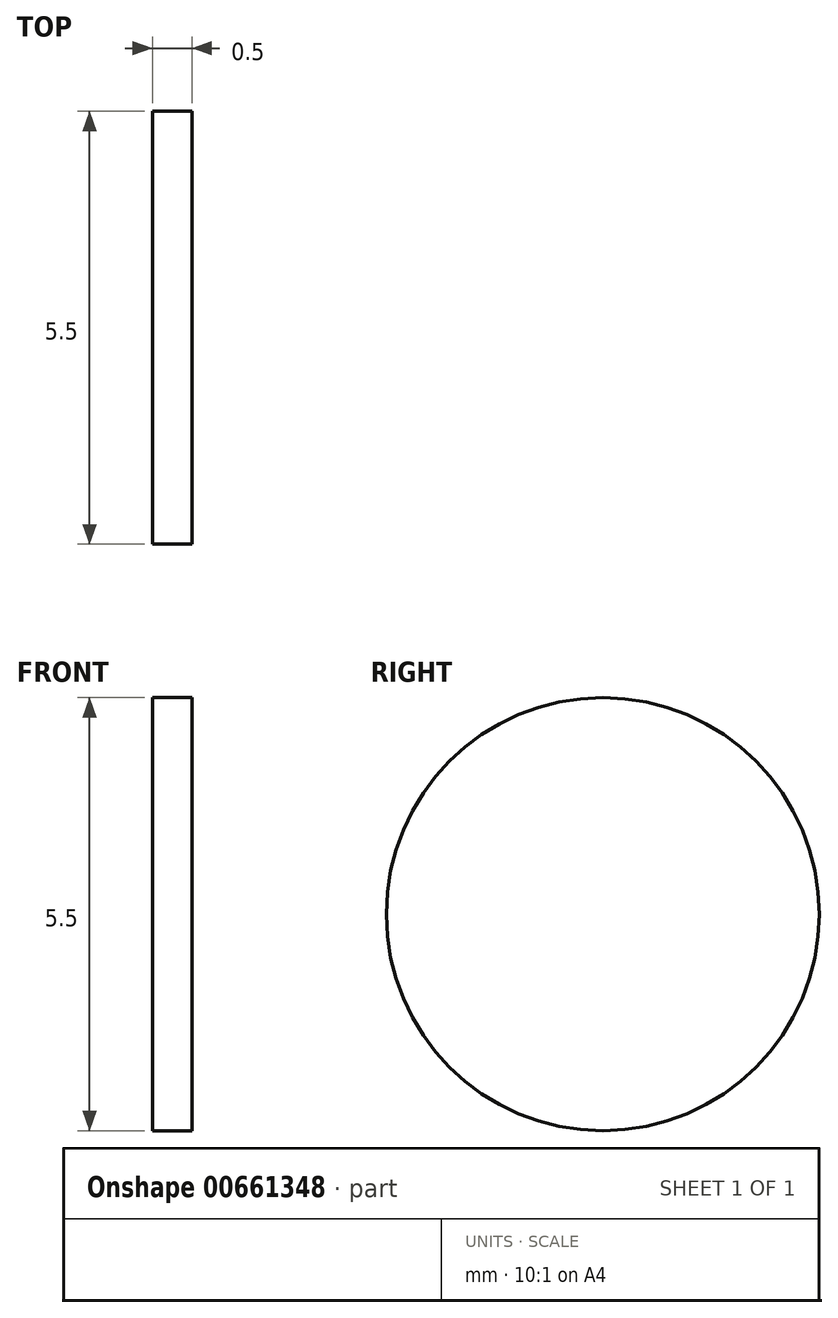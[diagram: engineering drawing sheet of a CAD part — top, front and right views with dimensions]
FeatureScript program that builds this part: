
annotation { "Feature Type Name" : "Feature", "Feature Type Description" : "" }
export const myFeature = defineFeature(function(context is Context, id is Id, definition is map)
    precondition{}
    {
        {
            var Q0;
            Q0=qCreatedBy(makeId("Right.planeOp"),FACE);
            var sketch = newSketch(context, id + "F0", { "sketchPlane" : qUnion([Q0])});
            skCircle(sketch, "E0", {"center": v(0, 0) * mm, "radius": 2.75 * mm});
            skSolve(sketch);
        }
        {
            var Q0;
            Q0=makeQuery(id+"F0.imprint","IMPRINT",FACE,{"disambiguationData":[TD([[makeQuery(id+"F0.imprint","IMPRINT",EDGE,{"derivedFrom":sQuery(id+"F0.wireOp",EDGE,"E0")}),1.0]])]});
            extrude(context, id + "F1", {"entities" : qUnion([Q0]), "endBound" : BoundingType.SYMMETRIC, "oppositeDirection" : true, "depth" : .5 * mm, "offsetDistance" : 25 * mm});
        }
    });
